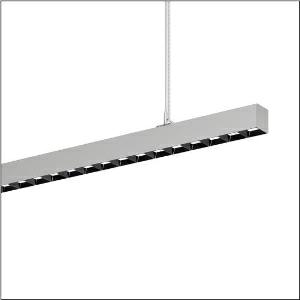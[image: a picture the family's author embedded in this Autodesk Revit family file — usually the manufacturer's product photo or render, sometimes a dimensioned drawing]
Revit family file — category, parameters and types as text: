
# Revit family: silica_r__21_51mx34dc3dsb_1a3f
name_source: partatom
category: Lighting Fixtures
units: mm (PartAtom-declared; Revit-internal decimal feet)

## family parameters
Cut with Voids When Loaded = No
Host = Face
Light Source = No
Part Type = Normal
Room Calculation Point = No
Round Connector Dimension = Use Diameter
Shared = No

## types (1)
- --- (1 x LED, 19200 lm, 129.1 W, 3000K)
    Apparent Load = 129 VA
    CIE Flux Codes = 74 94 99 56 100
    Color Rendering = 80
    Color Temperature = 3000K
    Default Elevation = 1800 mm
    Description = Silica® 21, office luminaire, primary light control with darklight reflector, of PMMA, black, light emission: direct/indirect distribution, primary light characteristic: asymmetric, installation type: suspended mounting, LED, rated luminous flux: 19.200lm, luminous efficacy: 149lm/W, light colour: 830, colour temperature: 3000K, with terminal, 3+2-pole, max. 2.5mm², mains connection: 220..240V, AC, 50/60Hz, rated input power: 129.1W, luminaire housing, of aluminium, metallic grey (RAL 9006), length: 3.004mm, width: 53mm, height: 53mm, protection rating (complete): IP20, insulation class (complete): insulation class I (protective earthing), certification: CE, permissible operating ambient temperature: 0..+35°C, standard: EN 50419, packaging unit: 1 piece
    Height = 53 mm
    Lamp = 1 x LED
    Lamp Light Flux = 19200 lm
    Lamp Power = 129.1 W
    Lamp count = 1
    Length = 3004 mm
    Luminous efficacy = 149 lm/W
    Manufacturer = Siteco
    ModVariant = No
    Model = 51MX34DC3DSB
    Mounting Place = Ceiling
    Mounting Type = Pendant
    Number of Poles = 1
    OnlyDefault = Yes
    Power Factor = 1
    Product Name = Silica® 21
    Product group = office luminaire | ceiling pendant
    ProductGroupID = 902
    Protection Class = Protection class I
    Protection Degree = IP 20
    RLX_Detail_Level = 1
    RLX_Emergency_Light_Flux = 0 lm
    RLX_Emergency_Type = 0
    RLX_Emergency_Type_DB = No
    RlxData = <blob elided: 66477 chars, md5=216978a8>
    Socket = socket
    Standby Power = 0 W
    System Light Flux = 19200 lm
    System Power = 129 W
    Type Comments = factory setting: luminous flux: 100 % | dim-lin: 254 | 448 mA
    Type Image = l_1313642.jpg
    URL = http://relux.com
    VarID = @adj_068695
    Voltage = 0 V
    Weight = 0.00 kg
    Width = 53 mm

## geometry (parser evidence)
native form markers: Blend x4, Sweep x12
no freeform markers — native parametric forms only
